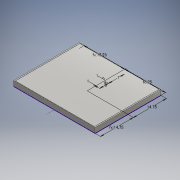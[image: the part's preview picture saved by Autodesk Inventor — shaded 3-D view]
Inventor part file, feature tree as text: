
AUTODESK INVENTOR PART (.ipt)
format: ipt  version: 2016 (Build 200138000, 138)  size: 116,736 bytes
history: native  units: mm
features: extrude x3, sketch x2, other x1
ambient origin geometry x8: Origin, YZ Plane, XZ Plane, XY Plane, X Axis, Y Axis, Z Axis, Center Point
bodies: Body1 (feature_tree)
feature tree (6):
  other  "ソリッド1"
  sketch  "スケッチ1"
  extrude  "押し出し1"  Depth=18.25mm
  extrude  "押し出し2"  Depth=18.25mm
  extrude  "押し出し5"  Depth=14.75mm
  sketch  "スケッチ2"
